# Revit family: 304_9555P-_
name_source: partatom
category: Pipe Accessories
revit_build: Autodesk Revit 2018 (Build: 20170223_1515(x64)
units: mm (PartAtom-declared; Revit-internal decimal feet)

## family parameters
Always vertical = Yes
Cut with Voids When Loaded = No
Part Type = Valve - Breaks Into
Round Connector Dimension = Use Diameter
Shared = No
Work Plane-Based = No

## types (8) — shared parameters
CAT0 = Yes
Description = Variable orifice cast iron double regulating valve PN16
L2D = 350 mm
L2D_Min = 3048 mm
Manufacturer = VIR
QmdConnectorList = 301;D;302;D
URL = http://www.vironline.com
W2D = 100 mm
magiPartTypeId = 304
magiProductFamilyId = 9555P-*

## per-type parameters (varying)
| type | D | F | H1 | H2 | H3 | H4 | L2 | L3 | L3__ve | L4 | L5 | R1 | R2 | R3 | R4 | R5 | V | WH | magiProductId |
| 9555P DN100 | 100 mm | 220 mm | 113 mm | 28 mm  [stored 0.0918635 ft] | 40 mm | 11 mm  [stored 0.0360892 ft] | 175 mm | 25 mm  [stored 0.082021 ft] | -25 mm | 252 mm | 49 mm  [stored 0.160761 ft] | 62 mm | 53 mm | 79 mm | 51 mm | 26 mm  [stored 0.0853018 ft] | 130 mm | 23 mm | F9500I100.1959 |
| 9555P DN125 | 125 mm | 250 mm | 129 mm | 32 mm | 45 mm | 10 mm  [stored 0.0328084 ft] | 200 mm | 28 mm  [stored 0.0918635 ft] | -28 mm  [stored -0.0918635 ft] | 288 mm | 56 mm  [stored 0.183727 ft] | 70 mm | 60 mm  [stored 0.19685 ft] | 90 mm | 58 mm | 26 mm  [stored 0.0853018 ft] | 130 mm | 23 mm | F9500I125.1959 |
| 9555P DN150 | 150 mm | 285 mm | 147 mm | 37 mm  [stored 0.121391 ft] | 51 mm | 10 mm  [stored 0.0328084 ft] | 240 mm | 34 mm | -34 mm | 346 mm | 67 mm | 80 mm | 68 mm | 103 mm | 67 mm | 26 mm  [stored 0.0853018 ft] | 130 mm | 23 mm | F9500I150.1959 |
| 9555P DN200 | 200 mm | 340 mm | 175 mm | 44 mm | 61 mm | 72 mm | 300 mm | 42 mm  [stored 0.137795 ft] | -42 mm  [stored -0.137795 ft] | 432 mm | 84 mm | 95 mm | 82 mm | 122 mm | 80 mm | 62 mm | 310 mm | 56 mm  [stored 0.183727 ft] | F9500I200.1959 |
| 9555P DN250 | 250 mm | 405 mm | 208 mm | 52 mm | 73 mm | 72 mm | 365 mm | 51 mm | -51 mm | 526 mm | 102 mm | 113 mm | 97 mm | 146 mm | 95 mm | 62 mm | 310 mm | 56 mm  [stored 0.183727 ft] | F9500I250.1959 |
| 9555P DN300 | 300 mm | 460 mm | 237 mm | 59 mm | 83 mm | 37 mm  [stored 0.121391 ft] | 425 mm | 60 mm  [stored 0.19685 ft] | -60 mm | 612 mm | 119 mm | 129 mm | 110 mm | 166 mm | 108 mm | 62 mm | 310 mm | 56 mm  [stored 0.183727 ft] | F9500I300.1959 |
| 9555P DN65 | 65 mm | 185 mm | 95 mm | 24 mm | 33 mm | 10 mm  [stored 0.0328084 ft] | 145 mm | 20 mm  [stored 0.0656168 ft] | -20 mm | 209 mm | 41 mm | 52 mm | 44 mm | 67 mm | 43 mm | 26 mm  [stored 0.0853018 ft] | 130 mm | 23 mm | F9500I065.1959 |
| 9555P DN80 | 80 mm | 200 mm | 103 mm | 26 mm  [stored 0.0853018 ft] | 36 mm | 5 mm  [stored 0.0164042 ft] | 155 mm | 22 mm | -22 mm | 223 mm | 43 mm | 56 mm  [stored 0.183727 ft] | 48 mm  [stored 0.15748 ft] | 72 mm | 47 mm | 26 mm  [stored 0.0853018 ft] | 130 mm | 23 mm | F9500I080.1959 |

note: column(s) folded — value = type name in every type: MC Product Code

note: [stored X ft] marks values corroborated as IEEE doubles in the binary element streams (Revit-internal decimal feet)

## geometry (parser evidence)
native form markers: Sweep x2
no freeform markers — native parametric forms only
